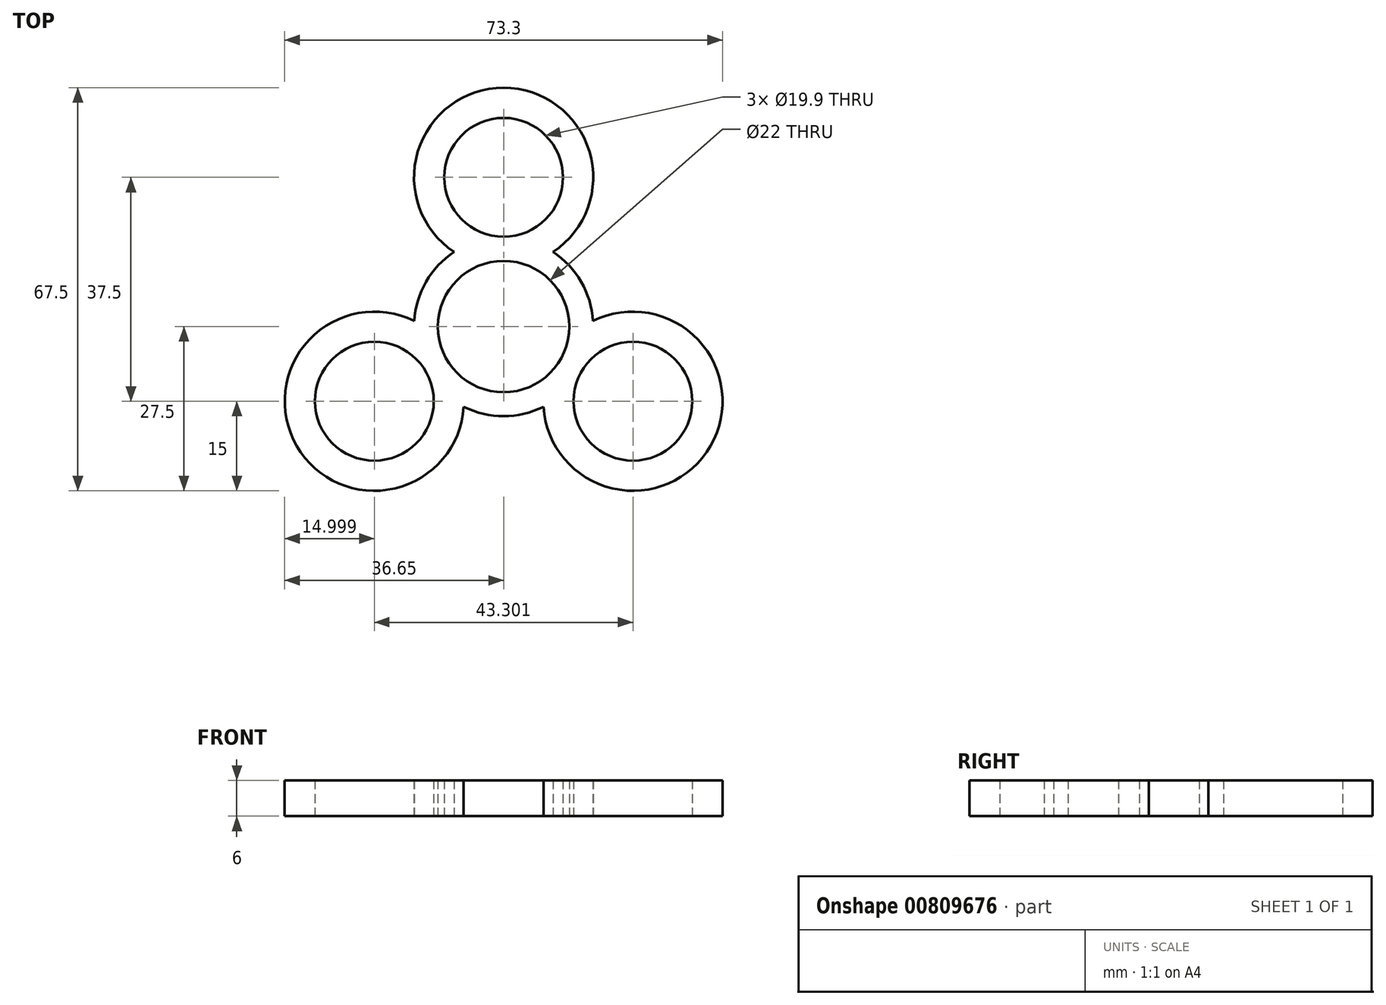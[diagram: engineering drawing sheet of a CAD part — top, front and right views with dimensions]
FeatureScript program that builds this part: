
annotation { "Feature Type Name" : "Feature", "Feature Type Description" : "" }
export const myFeature = defineFeature(function(context is Context, id is Id, definition is map)
    precondition{}
    {
        {
            var Q0;
            Q0=qCreatedBy(makeId("Top.planeOp"),FACE);
            var sketch = newSketch(context, id + "F0", { "sketchPlane" : qUnion([Q0])});
            skArc(sketch, "E0", {"start": v(9.53, 5.5) * mm, "mid": v(0, 11) * mm, "end": v(-9.53, 5.5) * mm});
            skCircle(sketch, "E1", {"center": v(0, 25) * mm, "radius": 9.95 * mm});
            skArc(sketch, "E2", {"start": v(8.3, 12.5) * mm, "mid": v(0, 40) * mm, "end": v(-8.3, 12.5) * mm});
            skArc(sketch, "E3", {"start": v(-8.3, 12.5) * mm, "mid": v(-10.93, 10.27) * mm, "end": v(-13, 7.5) * mm});
            skArc(sketch, "E4.trimOffspring", {"start": v(13, 7.5) * mm, "mid": v(10.93, 10.27) * mm, "end": v(8.3, 12.5) * mm});
            skArc(sketch, "E5.1.0", {"start": v(-14.97, 0.93) * mm, "mid": v(-34.64, -20) * mm, "end": v(-6.68, -13.43) * mm});
            skCircle(sketch, "E5.1.1", {"center": v(-21.65, -12.5) * mm, "radius": 9.95 * mm});
            skArc(sketch, "E5.1.2", {"start": v(-6.68, -13.43) * mm, "mid": v(-3.43, -14.6) * mm, "end": v(0, -15) * mm});
            skArc(sketch, "E5.1.3", {"start": v(-9.53, 5.5) * mm, "mid": v(-9.53, -5.5) * mm, "end": v(0, -11) * mm});
            skArc(sketch, "E5.1.4", {"start": v(-13, 7.5) * mm, "mid": v(-14.36, 4.33) * mm, "end": v(-14.97, 0.93) * mm});
            skArc(sketch, "E5.2.0", {"start": v(6.68, -13.43) * mm, "mid": v(34.64, -20) * mm, "end": v(14.97, 0.93) * mm});
            skCircle(sketch, "E5.2.1", {"center": v(21.65, -12.5) * mm, "radius": 9.95 * mm});
            skArc(sketch, "E5.2.2", {"start": v(14.97, 0.93) * mm, "mid": v(14.36, 4.33) * mm, "end": v(13, 7.5) * mm});
            skArc(sketch, "E5.2.3", {"start": v(0, -11) * mm, "mid": v(9.53, -5.5) * mm, "end": v(9.53, 5.5) * mm});
            skArc(sketch, "E5.2.4", {"start": v(0, -15) * mm, "mid": v(3.43, -14.6) * mm, "end": v(6.68, -13.43) * mm});
            skSolve(sketch);
        }
        {
            var Q0;
            Q0 = qSketchRegion(id + "F0", true);
            extrude(context, id + "F1", {"entities" : qUnion([Q0]), "depth" : 6 * mm, "offsetDistance" : 25 * mm});
        }
    });
